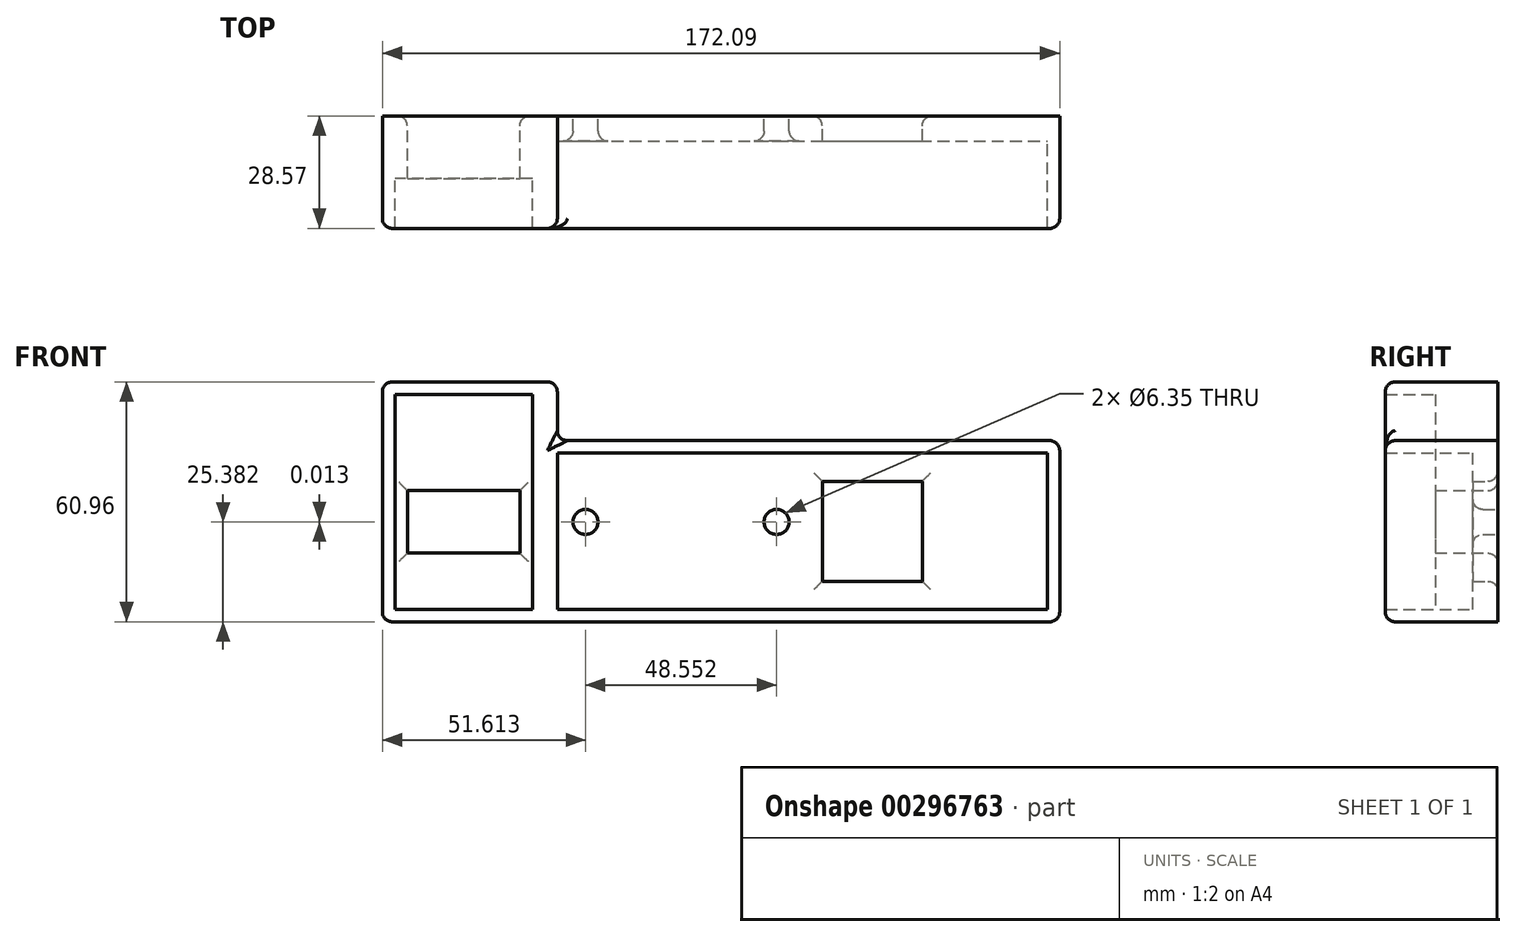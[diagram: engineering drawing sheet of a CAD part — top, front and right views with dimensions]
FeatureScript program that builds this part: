
annotation { "Feature Type Name" : "Feature", "Feature Type Description" : "" }
export const myFeature = defineFeature(function(context is Context, id is Id, definition is map)
    precondition{}
    {
        {
            var Q0;
            Q0=qCreatedBy(makeId("Front.planeOp"),FACE);
            var sketch = newSketch(context, id + "F0", { "sketchPlane" : qUnion([Q0])});
            skLineSegment(sketch, "E0.bottom", {"start": v(0, 0) * mm, "end": v(124.46, 0) * mm});
            skLineSegment(sketch, "E0.top", {"start": v(0, 39.69) * mm, "end": v(124.46, 39.69) * mm});
            skLineSegment(sketch, "E0.left", {"start": v(0, 0) * mm, "end": v(0, 39.69) * mm});
            skLineSegment(sketch, "E0.right", {"start": v(124.46, 0) * mm, "end": v(124.46, 39.69) * mm});
            skLineSegment(sketch, "E1.bottom", {"start": v(-6.35, 54.61) * mm, "end": v(-41.28, 54.6) * mm});
            skLineSegment(sketch, "E1.top", {"start": v(-6.35, 0) * mm, "end": v(-41.28, 0) * mm});
            skLineSegment(sketch, "E1.left", {"start": v(-6.35, 54.61) * mm, "end": v(-6.35, 0) * mm});
            skLineSegment(sketch, "E1.right", {"start": v(-41.28, 54.6) * mm, "end": v(-41.28, 0) * mm});
            skLineSegment(sketch, "E2.bottom", {"start": v(-44.45, 57.78) * mm, "end": v(0, 57.79) * mm});
            skLineSegment(sketch, "E2.top", {"start": v(-44.45, -3.18) * mm, "end": v(0, -3.17) * mm});
            skLineSegment(sketch, "E2.left", {"start": v(-44.45, 57.78) * mm, "end": v(-44.45, -3.18) * mm});
            skLineSegment(sketch, "E2.right", {"start": v(0, 57.79) * mm, "end": v(0, -3.17) * mm});
            skLineSegment(sketch, "E3.bottom", {"start": v(127.63, 42.86) * mm, "end": v(0, 42.86) * mm});
            skLineSegment(sketch, "E3.top", {"start": v(127.64, -3.17) * mm, "end": v(0, -3.17) * mm});
            skLineSegment(sketch, "E3.left", {"start": v(127.63, 42.86) * mm, "end": v(127.64, -3.17) * mm});
            skLineSegment(sketch, "E3.right", {"start": v(0, 42.86) * mm, "end": v(0, -3.17) * mm});
            skLineSegment(sketch, "E4.bottom", {"start": v(-38.1, 30.16) * mm, "end": v(-9.53, 30.16) * mm});
            skLineSegment(sketch, "E4.top", {"start": v(-38.1, 14.29) * mm, "end": v(-9.53, 14.29) * mm});
            skLineSegment(sketch, "E4.left", {"start": v(-38.1, 30.16) * mm, "end": v(-38.1, 14.29) * mm});
            skLineSegment(sketch, "E4.right", {"start": v(-9.53, 30.16) * mm, "end": v(-9.53, 14.29) * mm});
            skLineSegment(sketch, "E5.bottom", {"start": v(67.3, 32.55) * mm, "end": v(92.7, 32.55) * mm});
            skLineSegment(sketch, "E5.top", {"start": v(67.3, 7.15) * mm, "end": v(92.7, 7.15) * mm});
            skLineSegment(sketch, "E5.left", {"start": v(67.3, 32.55) * mm, "end": v(67.3, 7.15) * mm});
            skLineSegment(sketch, "E5.right", {"start": v(92.7, 32.55) * mm, "end": v(92.7, 7.15) * mm});
            skCircle(sketch, "E6", {"center": v(7.16, 22.21) * mm, "radius": 3.18 * mm});
            skCircle(sketch, "E7", {"center": v(55.71, 22.22) * mm, "radius": 3.18 * mm});
            skPoint(sketch, "E7.centerSnap0", {"position": v(-9.53, 22.22) * mm});
            skSolve(sketch);
        }
        {
            var Q0;
            Q0=makeQuery(id+"F0.imprint","IMPRINT",FACE,{"disambiguationData":[TD([[makeQuery(id+"F0.imprint","IMPRINT",EDGE,{"derivedFrom":sQuery(id+"F0.wireOp",EDGE,"E1.bottom")}),-1.0]])]});
            var Q1;
            {var subQ1=sQuery(id+"F0.wireOp",EDGE,"E0.bottom");Q1=makeQuery(id+"F0.imprint","IMPRINT",FACE,{"disambiguationData":[TD([[makeQuery(id+"F0.imprint","IMPRINT",EDGE,{"derivedFrom":subQ1}),-1.0]])]});}
            extrude(context, id + "F1", {"entities" : qUnion([Q0, Q1]), "depth" : 28.57 * mm});
        }
        {
            var Q0;
            {var subQ2=sQuery(id+"F0.wireOp",EDGE,"E0.bottom");Q0=makeQuery(id+"F0.imprint","IMPRINT",FACE,{"disambiguationData":[TD([[makeQuery(id+"F0.imprint","IMPRINT",EDGE,{"derivedFrom":subQ2}),1.0]])]});}
            extrude(context, id + "F2", {"entities" : qUnion([Q0]), "operationType" : NewBodyOperationType.ADD, "depth" : 6.35 * mm});
        }
        {
            var Q0;
            Q0=makeQuery(id+"F0.imprint","IMPRINT",FACE,{"disambiguationData":[TD([[makeQuery(id+"F0.imprint","IMPRINT",EDGE,{"derivedFrom":sQuery(id+"F0.wireOp",EDGE,"E1.bottom")}),1.0]])]});
            extrude(context, id + "F3", {"entities" : qUnion([Q0]), "operationType" : NewBodyOperationType.ADD, "depth" : 15.88 * mm});
        }
        {
            var Q0;
            Q0=makeQuery(id+"F1.opExtrude","CAP_EDGE",EDGE,{"disambiguationData":[OSD([sQuery(id+"F0.wireOp",EDGE,"E2.left")])],"isStart":false});
            var Q1;
            Q1=makeQuery(id+"F1.opExtrude","CAP_EDGE",EDGE,{"disambiguationData":[OSD([sQuery(id+"F0.wireOp",EDGE,"E2.bottom")])],"isStart":false});
            var Q2;
            Q2=makeQuery(id+"F1.opExtrude","CAP_EDGE",EDGE,{"disambiguationData":[OSD([sQuery(id+"F0.wireOp",EDGE,"E2.top"),sQuery(id+"F0.wireOp",EDGE,"E3.top")])],"isStart":false});
            var Q3;
            Q3=makeQuery(id+"F1.opExtrude","CAP_EDGE",EDGE,{"disambiguationData":[OSD([sQuery(id+"F0.wireOp",EDGE,"E3.bottom")])],"isStart":false});
            var Q4;
            Q4=makeQuery(id+"F1.opExtrude","CAP_EDGE",EDGE,{"disambiguationData":[OSD([sQuery(id+"F0.wireOp",EDGE,"E3.left")])],"isStart":false});
            var Q5;
            Q5=makeQuery(id+"F1.opExtrude","CAP_EDGE",EDGE,{"disambiguationData":[OSD([sQuery(id+"F0.wireOp",EDGE,"E2.right")])],"isStart":false});
            var Q6;
            Q6=makeQuery(id+"F2.opExtrude","CAP_EDGE",EDGE,{"disambiguationData":[OSD([sQuery(id+"F0.wireOp",EDGE,"E7")])],"isStart":false});
            var Q7;
            Q7=makeQuery(id+"F2.opExtrude","CAP_EDGE",EDGE,{"disambiguationData":[OSD([sQuery(id+"F0.wireOp",EDGE,"E6")])],"isStart":false});
            var Q8;
            Q8=makeQuery(id+"F2.opExtrude","CAP_EDGE",EDGE,{"disambiguationData":[OSD([sQuery(id+"F0.wireOp",EDGE,"E5.top")])],"isStart":true});
            var Q9;
            Q9=makeQuery(id+"F2.opExtrude","CAP_EDGE",EDGE,{"disambiguationData":[OSD([sQuery(id+"F0.wireOp",EDGE,"E5.right")])],"isStart":true});
            var Q10;
            Q10=makeQuery(id+"F2.opExtrude","CAP_EDGE",EDGE,{"disambiguationData":[OSD([sQuery(id+"F0.wireOp",EDGE,"E5.bottom")])],"isStart":true});
            var Q11;
            Q11=makeQuery(id+"F3.opExtrude","CAP_EDGE",EDGE,{"disambiguationData":[OSD([sQuery(id+"F0.wireOp",EDGE,"E4.top")])],"isStart":true});
            var Q12;
            Q12=makeQuery(id+"F3.opExtrude","CAP_EDGE",EDGE,{"disambiguationData":[OSD([sQuery(id+"F0.wireOp",EDGE,"E4.right")])],"isStart":true});
            var Q13;
            Q13=makeQuery(id+"F3.opExtrude","CAP_EDGE",EDGE,{"disambiguationData":[OSD([sQuery(id+"F0.wireOp",EDGE,"E4.bottom")])],"isStart":true});
            var Q14;
            Q14=makeQuery(id+"F3.opExtrude","CAP_EDGE",EDGE,{"disambiguationData":[OSD([sQuery(id+"F0.wireOp",EDGE,"E4.left")])],"isStart":true});
            var Q15;
            Q15=makeQuery(id+"F2.opExtrude","CAP_EDGE",EDGE,{"disambiguationData":[OSD([sQuery(id+"F0.wireOp",EDGE,"E5.left")])],"isStart":true});
            fillet(context, id + "F4", {"entities" : qUnion([Q0, Q1, Q2, Q3, Q4, Q5, Q6, Q7, Q8, Q9, Q10, Q11, Q12, Q13, Q14, Q15]), "radius" : 2.54 * mm, "tangentPropagation" : true, "allowEdgeOverflow" : false});
        }
        {
            var Q0;
            Q0=makeQuery(id+"F1.opExtrude","SWEPT_EDGE",EDGE,{"disambiguationData":[OSD([sQuery(id+"F0.wireOp",EDGE,"E2.top"),sQuery(id+"F0.wireOp",EDGE,"E2.left")])]});
            var Q1;
            Q1=makeQuery(id+"F1.opExtrude","SWEPT_EDGE",EDGE,{"disambiguationData":[OSD([sQuery(id+"F0.wireOp",EDGE,"E2.bottom"),sQuery(id+"F0.wireOp",EDGE,"E2.left")])]});
            var Q2;
            Q2=makeQuery(id+"F1.opExtrude","SWEPT_EDGE",EDGE,{"disambiguationData":[OSD([sQuery(id+"F0.wireOp",EDGE,"E2.bottom"),sQuery(id+"F0.wireOp",EDGE,"E2.right")])]});
            var Q3;
            Q3=makeQuery(id+"F1.opExtrude","SWEPT_EDGE",EDGE,{"disambiguationData":[OSD([sQuery(id+"F0.wireOp",EDGE,"E2.right"),sQuery(id+"F0.wireOp",EDGE,"E3.bottom"),sQuery(id+"F0.wireOp",EDGE,"E3.right")])]});
            var Q4;
            Q4=makeQuery(id+"F1.opExtrude","SWEPT_EDGE",EDGE,{"disambiguationData":[OSD([sQuery(id+"F0.wireOp",EDGE,"E3.top"),sQuery(id+"F0.wireOp",EDGE,"E3.left")])]});
            var Q5;
            Q5=makeQuery(id+"F1.opExtrude","SWEPT_EDGE",EDGE,{"disambiguationData":[OSD([sQuery(id+"F0.wireOp",EDGE,"E3.bottom"),sQuery(id+"F0.wireOp",EDGE,"E3.left")])]});
            fillet(context, id + "F5", {"entities" : qUnion([Q0, Q1, Q2, Q3, Q4, Q5]), "radius" : 2.54 * mm, "tangentPropagation" : true, "allowEdgeOverflow" : false});
        }
    });
